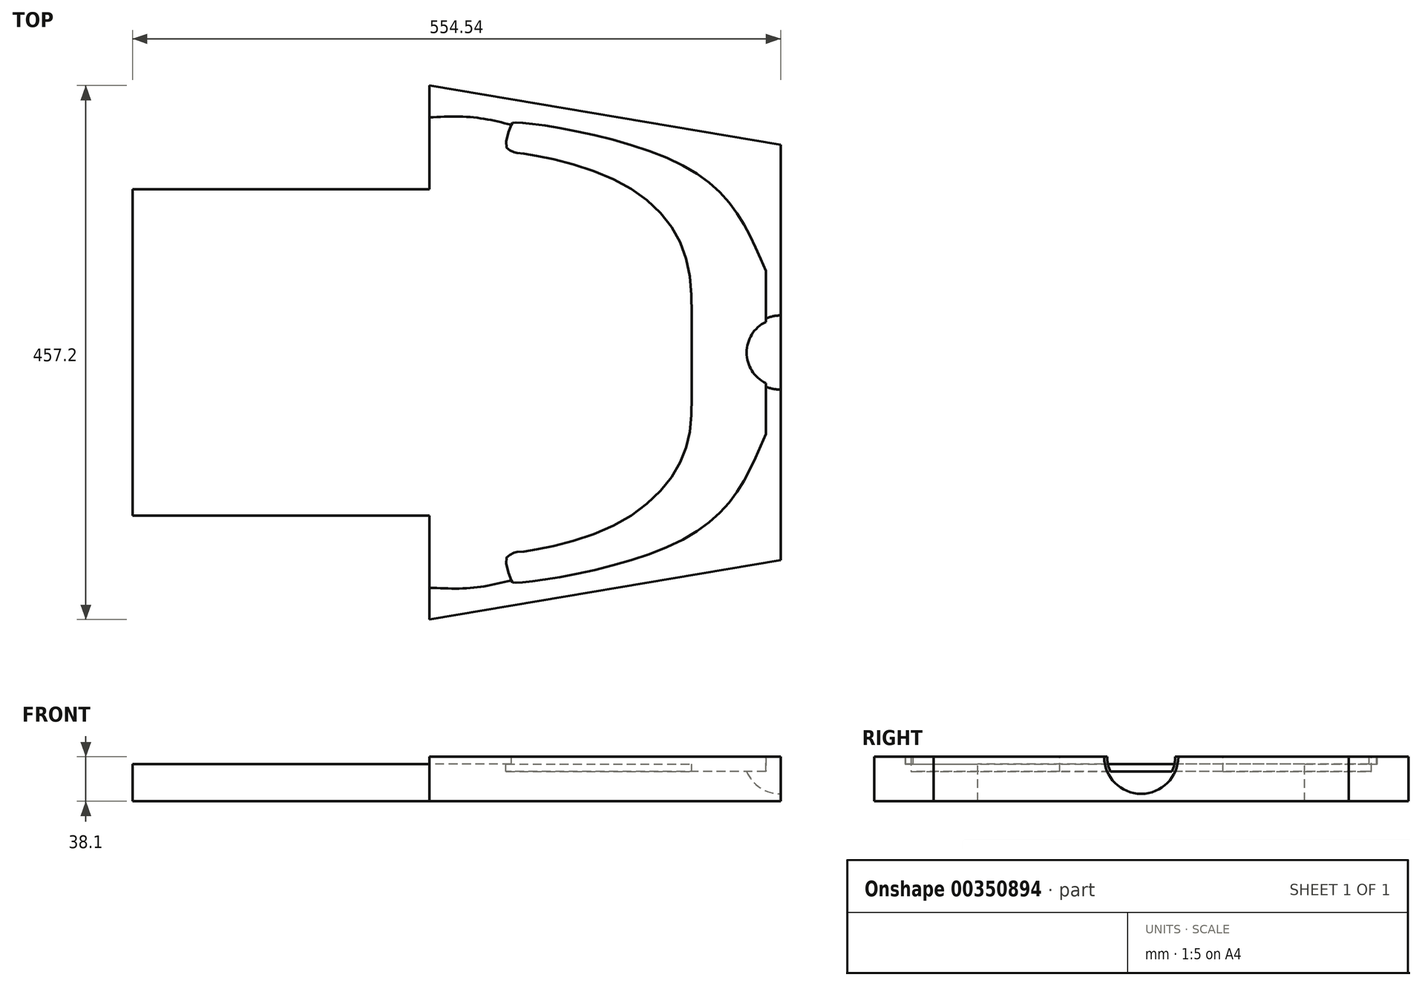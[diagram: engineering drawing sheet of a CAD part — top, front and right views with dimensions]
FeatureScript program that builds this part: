
annotation { "Feature Type Name" : "Feature", "Feature Type Description" : "" }
export const myFeature = defineFeature(function(context is Context, id is Id, definition is map)
    precondition{}
    {
        {
            var Q0;
            Q0=qCreatedBy(makeId("Top.planeOp"),FACE);
            var sketch = newSketch(context, id + "F0", { "sketchPlane" : qUnion([Q0])});
            skLineSegment(sketch, "E0", {"start": v(0, 0) * mm, "end": v(0, 457.2) * mm});
            skLineSegment(sketch, "E1", {"start": v(0, 457.2) * mm, "end": v(300.54, 406.4) * mm});
            skLineSegment(sketch, "E2", {"start": v(300.54, 406.4) * mm, "end": v(300.54, 50.8) * mm});
            skLineSegment(sketch, "E3", {"start": v(300.54, 50.8) * mm, "end": v(0, 0) * mm});
            skSolve(sketch);
        }
        {
            var Q0;
            Q0 = qSketchRegion(id + "F0", true);
            extrude(context, id + "F1", {"entities" : qUnion([Q0]), "depth" : 38.1 * mm});
        }
        {
            var Q0;
            Q0=makeQuery(id+"F1.opExtrude","CAP_FACE",FACE,{"disambiguationData":[OSD([sQuery(id+"F0.wireOp",EDGE,"E0"),sQuery(id+"F0.wireOp",EDGE,"E1"),sQuery(id+"F0.wireOp",EDGE,"E2"),sQuery(id+"F0.wireOp",EDGE,"E3")])],"isStart":false});
            var sketch = newSketch(context, id + "F2", { "sketchPlane" : qUnion([Q0])});
            skLineSegment(sketch, "E4", {"start": v(287.84, 228.6) * mm, "end": v(287.84, 158.75) * mm});
            skPoint(sketch, "E5", {"position": v(224.34, 228.6) * mm});
            skFitSpline(sketch, "E6", {"points": [v(287.84, 158.75) * mm, v(219.1, 69.58) * mm, v(73.24, 31.55) * mm, v(70.02, 33.56) * mm, v(65.59, 51.51) * mm, v(68.55, 55.13) * mm, v(72.98, 57.41) * mm, v(76.33, 57.82) * mm, v(150.55, 77.07) * mm, v(216.35, 138.02) * mm, v(224.34, 228.6) * mm], "startDerivative": vector(-245.23, -593.7) * mm, "endDerivative": vector(0, 814.5) * mm});
            skFitSpline(sketch, "E7.MirrorCS", {"points": [v(287.84, 298.45) * mm, v(219.1, 387.62) * mm, v(73.24, 425.65) * mm, v(70.02, 423.64) * mm, v(65.59, 405.69) * mm, v(68.55, 402.07) * mm, v(72.98, 399.79) * mm, v(76.33, 399.38) * mm, v(150.55, 380.13) * mm, v(216.35, 319.18) * mm, v(224.34, 228.6) * mm], "startDerivative": vector(-245.23, 593.7) * mm, "endDerivative": vector(0, -632.7) * mm});
            skLineSegment(sketch, "E8.MirrorCS", {"start": v(287.84, 228.6) * mm, "end": v(287.84, 298.45) * mm});
            skPoint(sketch, "E9.start.orphan", {"position": v(0, 228.6) * mm});
            skPoint(sketch, "E10", {"position": v(300.54, 228.6) * mm});
            skLineSegment(sketch, "E11", {"start": v(300.54, 228.6) * mm, "end": v(287.84, 228.6) * mm});
            skPoint(sketch, "E12", {"position": v(300.54, 196.85) * mm});
            skPoint(sketch, "E13", {"position": v(37.28, 27.23) * mm});
            skFitSpline(sketch, "E14", {"points": [v(70.02, 33.56) * mm, v(37.28, 27.23) * mm, v(0, 27.23) * mm], "startDerivative": vector(-66.1, -16.17) * mm, "endDerivative": vector(-73.88, 3.34) * mm});
            skFitSpline(sketch, "E15.MirrorCS", {"points": [v(70.02, 423.64) * mm, v(37.28, 429.97) * mm, v(0, 429.97) * mm], "startDerivative": vector(-66.1, 16.17) * mm, "endDerivative": vector(-73.88, -3.34) * mm});
            skSolve(sketch);
        }
        {
            var Q0;
            Q0 = qSketchRegion(id + "F2", true);
            extrude(context, id + "F3", {"entities" : qUnion([Q0]), "operationType" : NewBodyOperationType.REMOVE, "oppositeDirection" : true, "depth" : 12.7 * mm});
        }
        {
            var Q0;
            Q0=makeQuery(id+"F1.opExtrude","CAP_FACE",FACE,{"disambiguationData":[OSD([sQuery(id+"F0.wireOp",EDGE,"E0"),sQuery(id+"F0.wireOp",EDGE,"E1"),sQuery(id+"F0.wireOp",EDGE,"E2"),sQuery(id+"F0.wireOp",EDGE,"E3")])],"isStart":false});
            var sketch = newSketch(context, id + "F4", { "sketchPlane" : qUnion([Q0])});
            skPoint(sketch, "E16", {"position": v(300.54, 228.6) * mm});
            skLineSegment(sketch, "E17", {"start": v(300.54, 196.85) * mm, "end": v(300.54, 228.6) * mm});
            skPoint(sketch, "E18", {"position": v(268.79, 228.6) * mm});
            skLineSegment(sketch, "E19", {"start": v(268.79, 228.6) * mm, "end": v(300.54, 228.6) * mm});
            skArc(sketch, "E20", {"start": v(300.54, 196.85) * mm, "mid": v(278.09, 206.15) * mm, "end": v(268.79, 228.6) * mm});
            skSolve(sketch);
        }
        {
            var Q0;
            Q0 = qSketchRegion(id + "F4", true);
            var Q1;
            Q1=sQuery(id+"F4.wireOp",EDGE,"E19");
            revolve(context, id + "F5", {"operationType" : NewBodyOperationType.REMOVE, "entities" : qUnion([Q0]), "axis" : qUnion([Q1]), "revolveType" : RevolveType.ONE_DIRECTION, "angle" : 180 * degree});
        }
        {
            var Q0;
            {var subQ4=sQuery(id+"F2.wireOp",EDGE,"E14");Q0=makeQuery(id+"F2.imprint","IMPRINT",FACE,{"disambiguationData":[TD([[makeQuery(id+"F2.imprint","IMPRINT",EDGE,{"derivedFrom":subQ4}),-1.0]])]});}
            extrude(context, id + "F6", {"entities" : qUnion([Q0]), "operationType" : NewBodyOperationType.REMOVE, "oppositeDirection" : true, "depth" : 6.35 * mm});
        }
        {
            var Q0;
            Q0=makeQuery(id+"F6.boolean.opBoolean","COPY",FACE,{"derivedFrom":makeQuery(id+"F6.opExtrude","CAP_FACE",FACE,{"disambiguationData":[OSD([sQuery(id+"F0.wireOp",EDGE,"E0"),sQuery(id+"F2.wireOp",EDGE,"E6"),sQuery(id+"F2.wireOp",EDGE,"E7.MirrorCS"),sQuery(id+"F2.wireOp",EDGE,"E14"),sQuery(id+"F2.wireOp",EDGE,"E15.MirrorCS")])],"isStart":false})});
            var sketch = newSketch(context, id + "F7", { "sketchPlane" : qUnion([Q0])});
            skPoint(sketch, "E21.startSnap0", {"position": v(0, 228.6) * mm});
            skPoint(sketch, "E22", {"position": v(0, 368.3) * mm});
            skPoint(sketch, "E23", {"position": v(0, 88.9) * mm});
            skLineSegment(sketch, "E24", {"start": v(0, 368.3) * mm, "end": v(0, 228.6) * mm});
            skLineSegment(sketch, "E25", {"start": v(0, 88.9) * mm, "end": v(0, 228.6) * mm});
            skLineSegment(sketch, "E26", {"start": v(0, 368.3) * mm, "end": v(-254, 368.3) * mm});
            skLineSegment(sketch, "E27", {"start": v(-254, 368.3) * mm, "end": v(-254, 88.9) * mm});
            skLineSegment(sketch, "E28", {"start": v(-254, 88.9) * mm, "end": v(0, 88.9) * mm});
            skSolve(sketch);
        }
        {
            var Q0;
            Q0=makeQuery(id+"F7.imprint","IMPRINT",FACE,{"disambiguationData":[TD([[makeQuery(id+"F7.imprint","IMPRINT",EDGE,{"derivedFrom":sQuery(id+"F7.wireOp",EDGE,"E24")}),1.0]])]});
            extrude(context, id + "F8", {"entities" : qUnion([Q0]), "operationType" : NewBodyOperationType.ADD, "oppositeDirection" : true, "depth" : 31.75 * mm});
        }
    });
